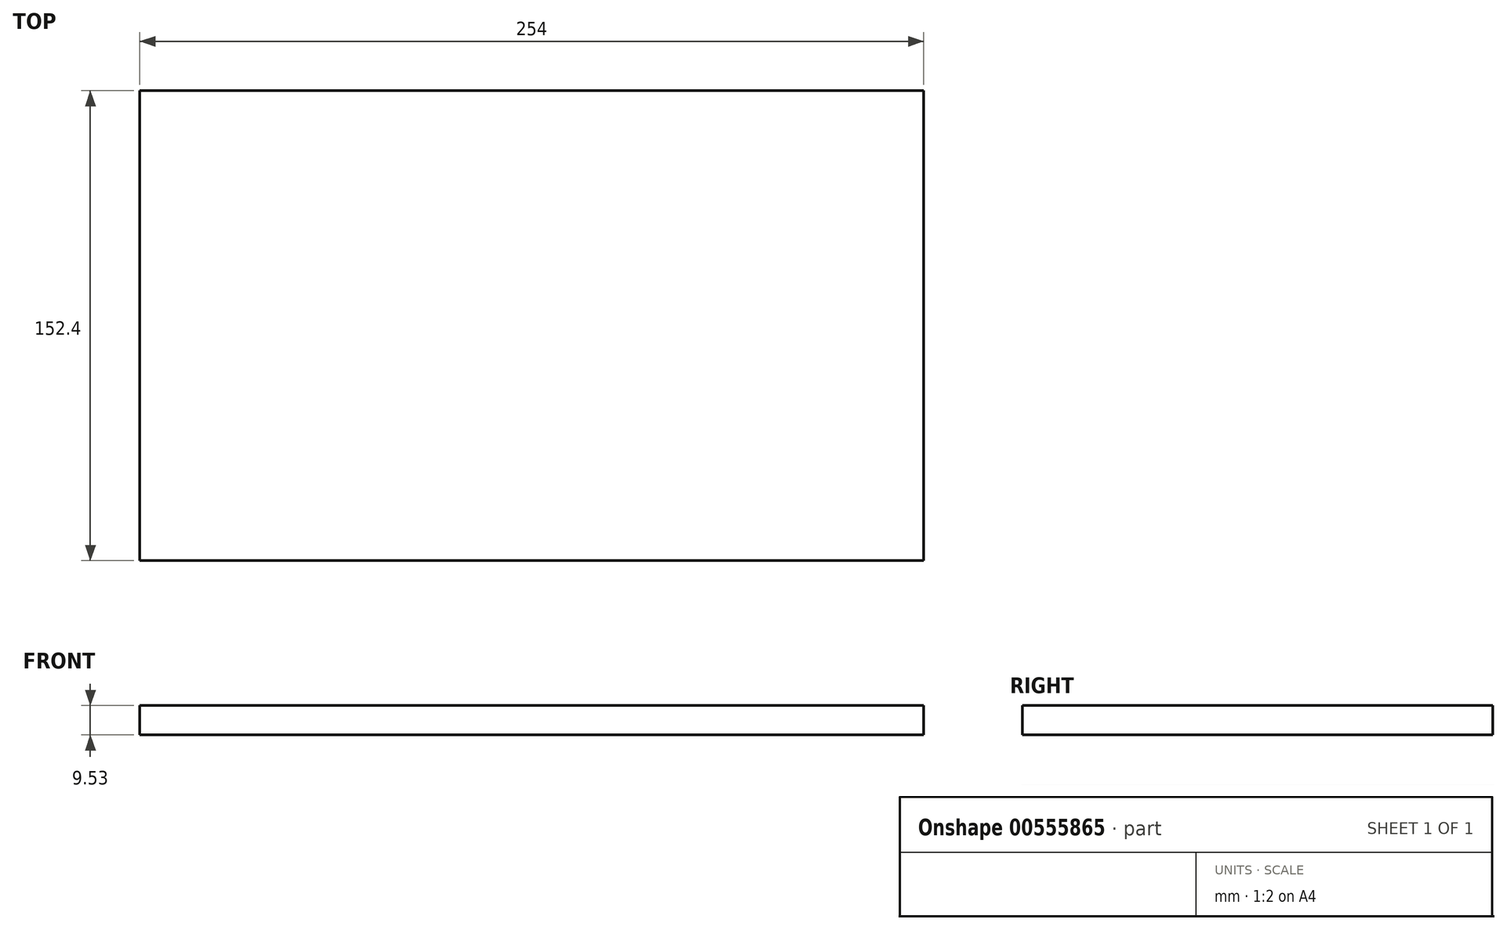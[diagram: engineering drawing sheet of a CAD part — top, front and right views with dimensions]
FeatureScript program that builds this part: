
annotation { "Feature Type Name" : "Feature", "Feature Type Description" : "" }
export const myFeature = defineFeature(function(context is Context, id is Id, definition is map)
    precondition{}
    {
        {
            var Q0;
            Q0=qCreatedBy(makeId("Top.planeOp"),FACE);
            var sketch = newSketch(context, id + "F0", { "sketchPlane" : qUnion([Q0])});
            skLineSegment(sketch, "E0.bottom", {"start": v(-127, 76.2) * mm, "end": v(127, 76.2) * mm});
            skLineSegment(sketch, "E0.top", {"start": v(-127, -76.2) * mm, "end": v(127, -76.2) * mm});
            skLineSegment(sketch, "E0.left", {"start": v(-127, 76.2) * mm, "end": v(-127, -76.2) * mm});
            skLineSegment(sketch, "E0.right", {"start": v(127, 76.2) * mm, "end": v(127, -76.2) * mm});
            skPoint(sketch, "E0.middle", {"position": v(0, 0) * mm});
            skSolve(sketch);
        }
        {
            var Q0;
            Q0=makeQuery(id+"F0.imprint","IMPRINT",FACE,{"disambiguationData":[TD([[makeQuery(id+"F0.imprint","IMPRINT",EDGE,{"derivedFrom":sQuery(id+"F0.wireOp",EDGE,"E0.bottom")}),-1.0]])]});
            extrude(context, id + "F1", {"entities" : qUnion([Q0]), "depth" : 9.52 * mm, "offsetDistance" : 25.4 * mm});
        }
    });
